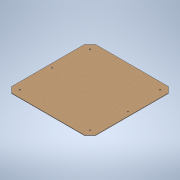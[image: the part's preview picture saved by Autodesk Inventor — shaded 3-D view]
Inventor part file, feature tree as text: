
AUTODESK INVENTOR PART (.ipt)
format: ipt  version: 2022 (Build 260153000, 153)  size: 146,944 bytes
history: native  units: mm
features: sketch x4, extrude x2, hole x2, other x1
ambient origin geometry x8: Origin, YZ Plane, XZ Plane, XY Plane, X Axis, Y Axis, Z Axis, Center Point
bodies: Body1 (feature_tree)
feature tree (9):
  other  "Sólido1"
  extrude  "Extrusão1"  Depth=4.0mm
  hole  "Furo1"  [1 undecoded]
  hole  "Furo2"  [1 undecoded]
  extrude  "Extrusão2"  Depth=40.0mm
  sketch  "Esboço1"  dims[d2=3.0mm d3=0.0mm]
  sketch  "Esboço2"  dims[d4=8.0mm d5=6.0mm d6=4.0mm d7=2.0mm d8=90.0deg d9=8.0mm d10=20.594885mm]
  sketch  "Esboço3"  dims[d11=8.0mm d12=6.0mm d13=4.0mm d14=2.0mm d15=90.0deg d16=8.0mm d17=20.594885mm d18=29.956mm]
  sketch  "Esboço4"  dims[d19=29.956mm d20=40.0mm d21=45.0deg d22=40.0mm d23=0.0mm d24=0.0mm]
note: 2 required parameter values undecoded (feature->parameter linkage not recoverable at this tier; creation-order binding heuristic only, values carry confidence <= 0.55)
